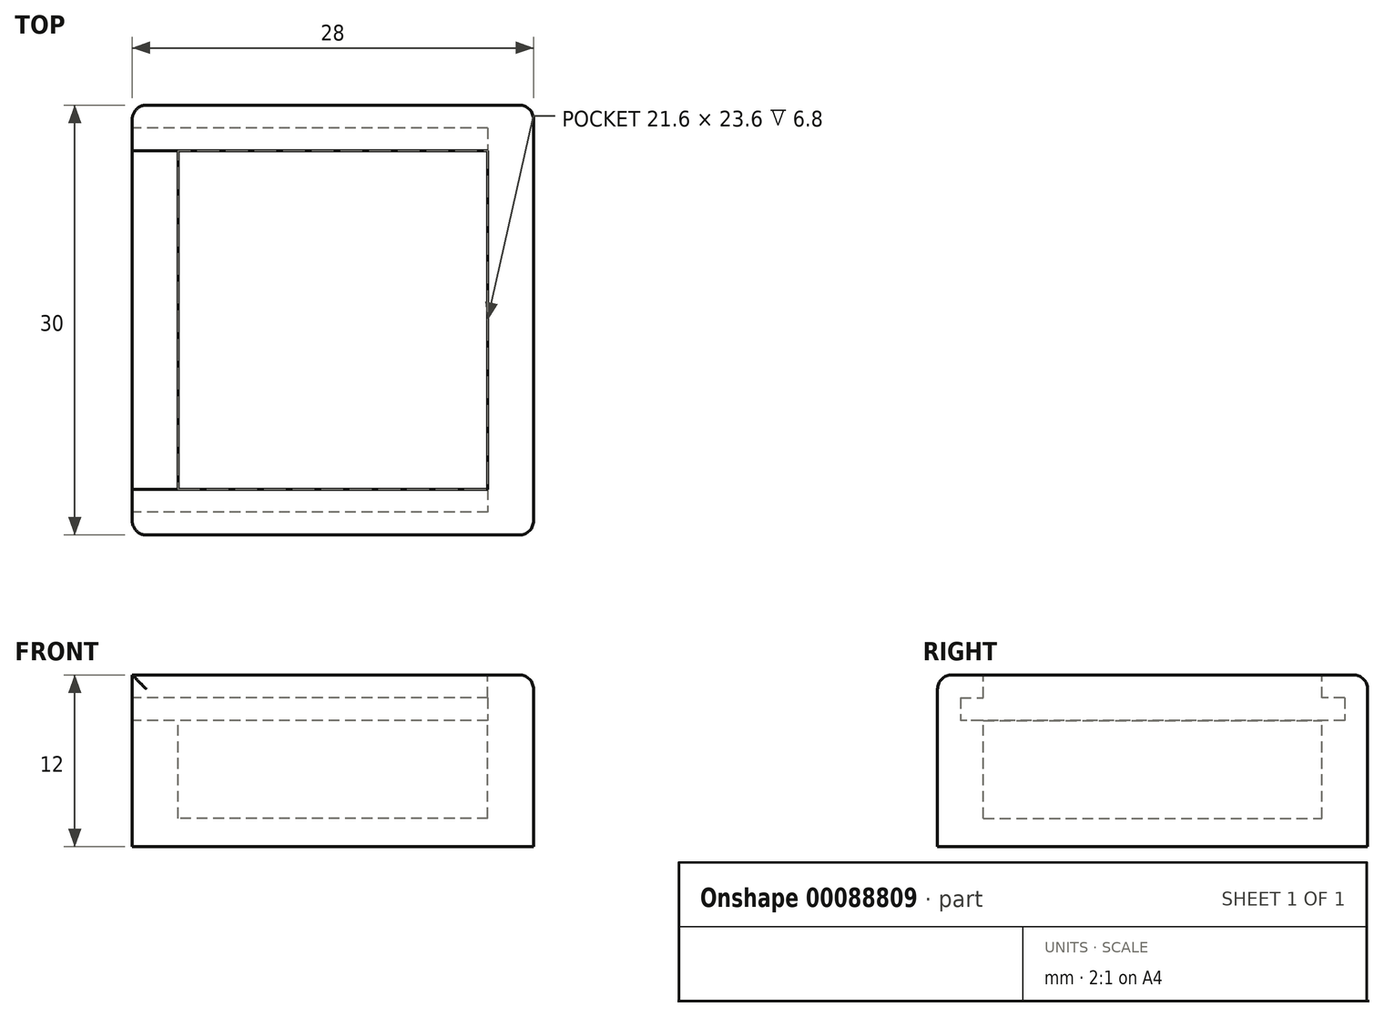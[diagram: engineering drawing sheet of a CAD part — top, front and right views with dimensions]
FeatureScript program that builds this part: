
annotation { "Feature Type Name" : "Feature", "Feature Type Description" : "" }
export const myFeature = defineFeature(function(context is Context, id is Id, definition is map)
    precondition{}
    {
        {
            var Q0;
            Q0=qCreatedBy(makeId("Front.planeOp"),FACE);
            var sketch = newSketch(context, id + "F0", { "sketchPlane" : qUnion([Q0])});
            skLineSegment(sketch, "E0", {"start": v(0, 0) * mm, "end": v(28, 0) * mm});
            skLineSegment(sketch, "E1", {"start": v(28, 0) * mm, "end": v(28, 12) * mm});
            skLineSegment(sketch, "E2", {"start": v(28, 12) * mm, "end": v(0, 12) * mm});
            skLineSegment(sketch, "E3", {"start": v(0, 12) * mm, "end": v(0, 0) * mm});
            skSolve(sketch);
        }
        {
            var Q0;
            Q0=makeQuery(id+"F0.imprint","IMPRINT",FACE,{"disambiguationData":[TD([[makeQuery(id+"F0.imprint","IMPRINT",EDGE,{"derivedFrom":sQuery(id+"F0.wireOp",EDGE,"E0")}),1.0]])]});
            extrude(context, id + "F1", {"entities" : qUnion([Q0]), "depth" : 30 * mm});
        }
        {
            var Q0;
            Q0=makeQuery(id+"F1.opExtrude","SWEPT_FACE",FACE,{"disambiguationData":[OSD([sQuery(id+"F0.wireOp",EDGE,"E2")])]});
            var sketch = newSketch(context, id + "F2", { "sketchPlane" : qUnion([Q0])});
            skLineSegment(sketch, "E4.0", {"start": v(24.8, -3.2) * mm, "end": v(3.2, -3.2) * mm});
            skLineSegment(sketch, "E4.1", {"start": v(24.8, -26.8) * mm, "end": v(24.8, -3.2) * mm});
            skLineSegment(sketch, "E4.2", {"start": v(24.8, -26.8) * mm, "end": v(3.2, -26.8) * mm});
            skLineSegment(sketch, "E4.3", {"start": v(3.2, -26.8) * mm, "end": v(3.2, -3.2) * mm});
            skSolve(sketch);
        }
        {
            var Q0;
            Q0 = qSketchRegion(id + "F2", true);
            var Q1;
            Q1=makeQuery(id+"F2.imprint","IMPRINT",FACE,{"disambiguationData":[TD([[makeQuery(id+"F2.imprint","IMPRINT",EDGE,{"derivedFrom":sQuery(id+"F2.wireOp",EDGE,"E4.0")}),1.0]])]});
            extrude(context, id + "F3", {"entities" : qUnion([Q0, Q1]), "operationType" : NewBodyOperationType.REMOVE, "oppositeDirection" : true, "depth" : 10 * mm});
        }
        {
            var Q0;
            Q0=makeQuery(id+"F1.opExtrude","SWEPT_FACE",FACE,{"disambiguationData":[OSD([sQuery(id+"F0.wireOp",EDGE,"E3")])]});
            var sketch = newSketch(context, id + "F4", { "sketchPlane" : qUnion([Q0])});
            skLineSegment(sketch, "E5", {"start": v(0, 12) * mm, "end": v(1.6, 12) * mm});
            skLineSegment(sketch, "E6", {"start": v(1.6, 12) * mm, "end": v(1.6, 10.4) * mm});
            skLineSegment(sketch, "E7", {"start": v(1.6, 10.4) * mm, "end": v(3.2, 10.4) * mm});
            skLineSegment(sketch, "E8", {"start": v(3.2, 10.4) * mm, "end": v(3.2, 12) * mm});
            skLineSegment(sketch, "E9", {"start": v(1.6, 10.4) * mm, "end": v(1.6, 8.8) * mm});
            skLineSegment(sketch, "E10", {"start": v(1.6, 8.8) * mm, "end": v(3.2, 8.8) * mm});
            skLineSegment(sketch, "E11", {"start": v(3.2, 8.8) * mm, "end": v(15, 8.8) * mm});
            skLineSegment(sketch, "E12.MirrorCS", {"start": v(26.8, 8.8) * mm, "end": v(15, 8.8) * mm});
            skLineSegment(sketch, "E13.MirrorCS", {"start": v(28.4, 8.8) * mm, "end": v(26.8, 8.8) * mm});
            skLineSegment(sketch, "E14.MirrorCS", {"start": v(28.4, 10.4) * mm, "end": v(26.8, 10.4) * mm});
            skLineSegment(sketch, "E15.MirrorCS", {"start": v(26.8, 10.4) * mm, "end": v(26.8, 12) * mm});
            skLineSegment(sketch, "E16.MirrorCS", {"start": v(28.4, 10.4) * mm, "end": v(28.4, 8.8) * mm});
            skSolve(sketch);
        }
        {
            var Q0;
            Q0=makeQuery(id+"F4.imprint","IMPRINT",FACE,{"disambiguationData":[TD([[makeQuery(id+"F4.imprint","IMPRINT",EDGE,{"derivedFrom":sQuery(id+"F4.wireOp",EDGE,"E7")}),-1.0]])]});
            var Q1;
            Q1=makeQuery(id+"F3.boolean.opBoolean","COPY",FACE,{"derivedFrom":makeQuery(id+"F3.opExtrude","SWEPT_FACE",FACE,{"disambiguationData":[OSD([sQuery(id+"F2.wireOp",EDGE,"E4.1")])]})});
            extrude(context, id + "F5", {"entities" : qUnion([Q0]), "operationType" : NewBodyOperationType.REMOVE, "endBound" : BoundingType.UP_TO_SURFACE, "oppositeDirection" : true, "endBoundEntityFace" : qUnion([Q1]), "depth" : 38.5 * mm});
        }
        {
            var Q0;
            Q0=makeQuery(id+"F1.opExtrude","CAP_EDGE",EDGE,{"disambiguationData":[OSD([sQuery(id+"F0.wireOp",EDGE,"E3")])],"isStart":true});
            var Q1;
            Q1=makeQuery(id+"F1.opExtrude","CAP_EDGE",EDGE,{"disambiguationData":[OSD([sQuery(id+"F0.wireOp",EDGE,"E2")])],"isStart":true});
            var Q2;
            Q2=makeQuery(id+"F1.opExtrude","CAP_EDGE",EDGE,{"disambiguationData":[OSD([sQuery(id+"F0.wireOp",EDGE,"E3")])],"isStart":false});
            var Q3;
            Q3=makeQuery(id+"F1.opExtrude","CAP_EDGE",EDGE,{"disambiguationData":[OSD([sQuery(id+"F0.wireOp",EDGE,"E2")])],"isStart":false});
            var Q4;
            Q4=makeQuery(id+"F1.opExtrude","CAP_EDGE",EDGE,{"disambiguationData":[OSD([sQuery(id+"F0.wireOp",EDGE,"E1")])],"isStart":true});
            var Q5;
            Q5=makeQuery(id+"F1.opExtrude","CAP_EDGE",EDGE,{"disambiguationData":[OSD([sQuery(id+"F0.wireOp",EDGE,"E1")])],"isStart":false});
            var Q6;
            Q6=makeQuery(id+"F1.opExtrude","SWEPT_EDGE",EDGE,{"disambiguationData":[OSD([sQuery(id+"F0.wireOp",EDGE,"E1"),sQuery(id+"F0.wireOp",EDGE,"E2")])]});
            fillet(context, id + "F6", {"entities" : qUnion([Q0, Q1, Q2, Q3, Q4, Q5, Q6]), "radius" : 1 * mm, "tangentPropagation" : true, "allowEdgeOverflow" : false});
        }
    });
